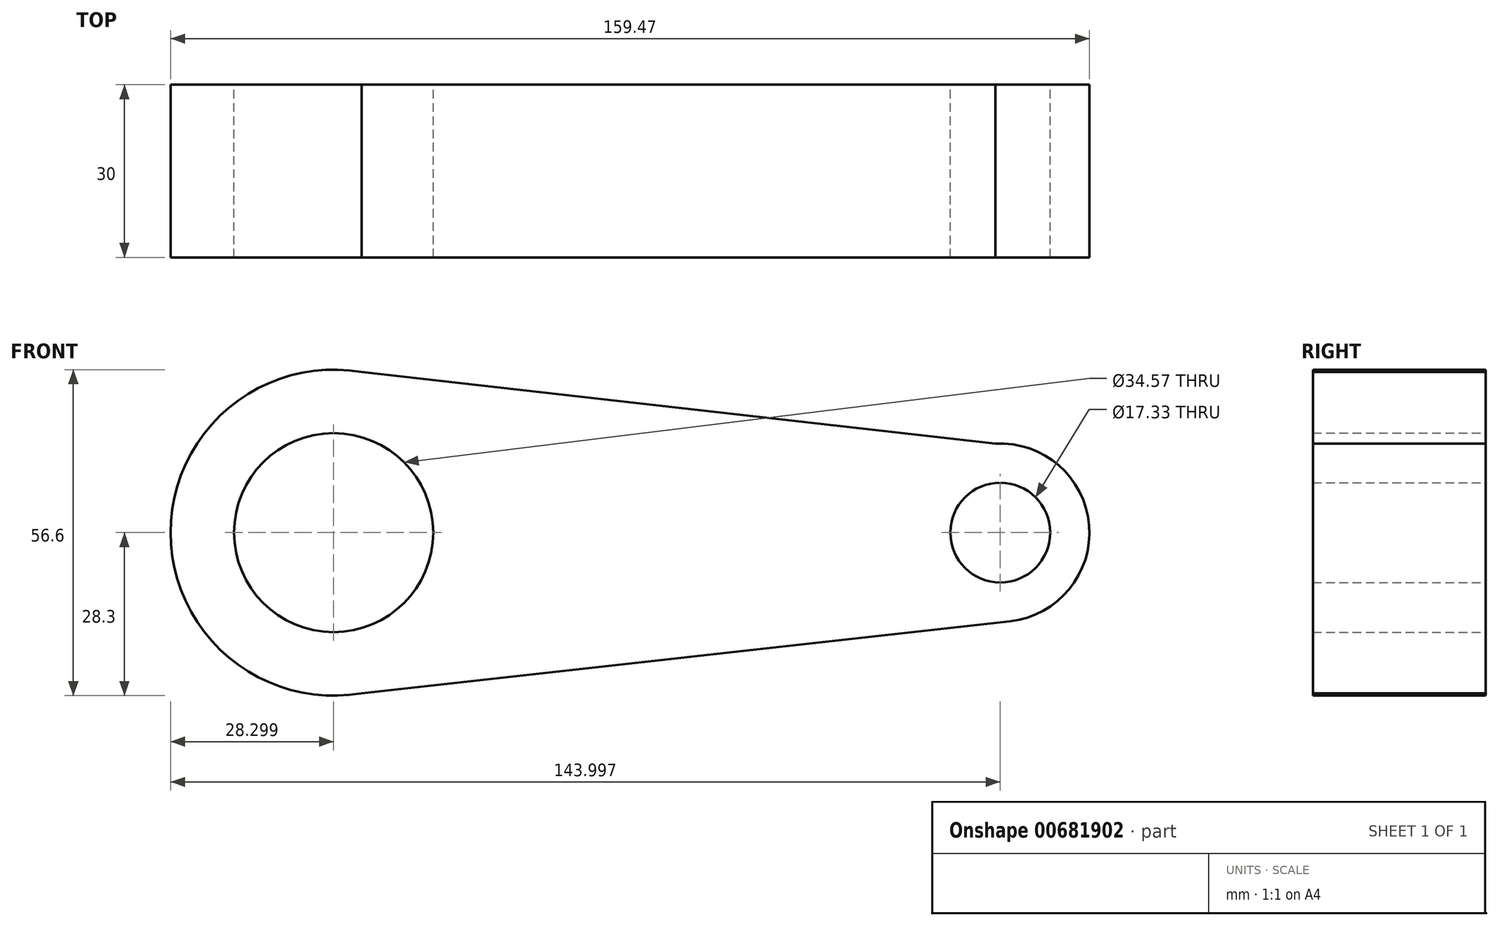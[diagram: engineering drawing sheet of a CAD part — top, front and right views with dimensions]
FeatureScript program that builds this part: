
annotation { "Feature Type Name" : "Feature", "Feature Type Description" : "" }
export const myFeature = defineFeature(function(context is Context, id is Id, definition is map)
    precondition{}
    {
        {
            var Q0;
            Q0=qCreatedBy(makeId("Front.planeOp"),FACE);
            var sketch = newSketch(context, id + "F0", { "sketchPlane" : qUnion([Q0])});
            skCircle(sketch, "E0", {"center": v(-58.28, 0) * mm, "radius": 28.3 * mm});
            skCircle(sketch, "E1", {"center": v(-58.28, 0) * mm, "radius": 17.28 * mm});
            skCircle(sketch, "E2", {"center": v(57.42, 0) * mm, "radius": 15.48 * mm});
            skCircle(sketch, "E3", {"center": v(57.42, 0) * mm, "radius": 8.66 * mm});
            skLineSegment(sketch, "E4", {"start": v(-53.43, 27.88) * mm, "end": v(56.54, 15.45) * mm});
            skLineSegment(sketch, "E5", {"start": v(-53.43, -27.88) * mm, "end": v(59.13, -15.38) * mm});
            skSolve(sketch);
        }
        {
            var Q0;
            Q0 = qSketchRegion(id + "F0", true);
            extrude(context, id + "F1", {"entities" : qUnion([Q0]), "depth" : 30 * mm, "offsetDistance" : 25 * mm});
        }
    });
